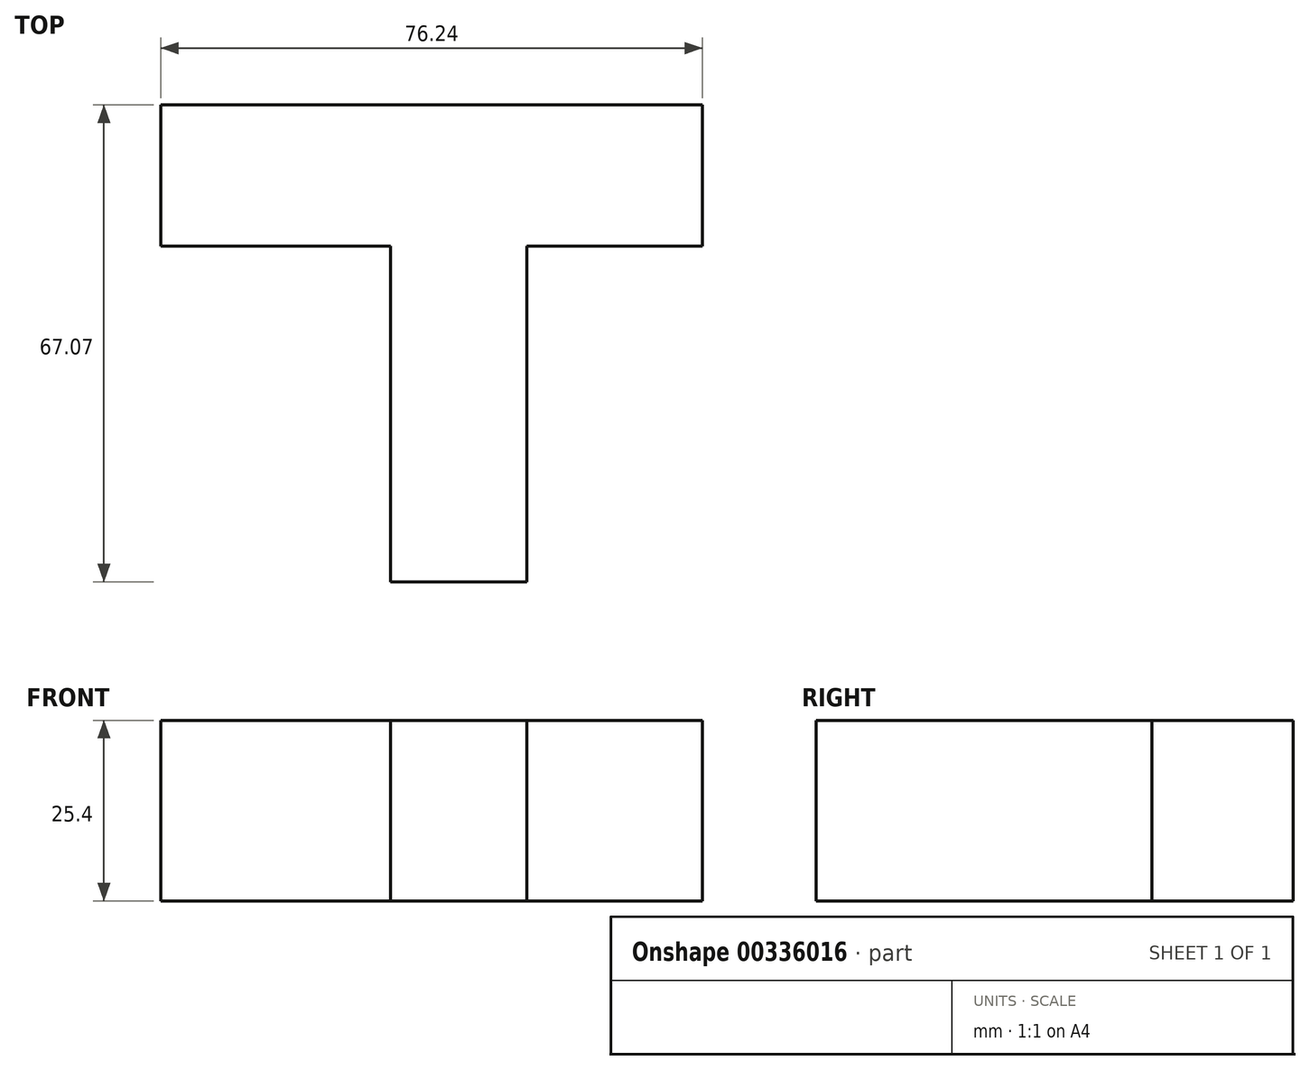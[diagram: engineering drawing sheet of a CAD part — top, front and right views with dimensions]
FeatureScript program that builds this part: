
annotation { "Feature Type Name" : "Feature", "Feature Type Description" : "" }
export const myFeature = defineFeature(function(context is Context, id is Id, definition is map)
    precondition{}
    {
        {
            var Q0;
            Q0=qCreatedBy(makeId("Top.planeOp"),FACE);
            var sketch = newSketch(context, id + "F0", { "sketchPlane" : qUnion([Q0])});
            skLineSegment(sketch, "E0", {"start": v(13.44, -28.7) * mm, "end": v(13.44, 18.55) * mm});
            skLineSegment(sketch, "E1", {"start": v(13.44, 18.55) * mm, "end": v(-18.88, 18.55) * mm});
            skLineSegment(sketch, "E2", {"start": v(-18.88, 18.55) * mm, "end": v(-18.88, 38.58) * mm});
            skLineSegment(sketch, "E3", {"start": v(-18.88, 38.58) * mm, "end": v(57.36, 38.58) * mm});
            skLineSegment(sketch, "E4", {"start": v(57.36, 38.38) * mm, "end": v(57.36, 18.55) * mm});
            skLineSegment(sketch, "E5", {"start": v(57.36, 18.55) * mm, "end": v(32.63, 18.55) * mm});
            skLineSegment(sketch, "E6", {"start": v(32.63, 18.55) * mm, "end": v(32.63, -28.7) * mm});
            skLineSegment(sketch, "E7", {"start": v(13.44, -28.7) * mm, "end": v(32.63, -28.7) * mm});
            skLineSegment(sketch, "E8.bottom", {"start": v(-18.88, 18.55) * mm, "end": v(57.36, 18.55) * mm});
            skLineSegment(sketch, "E8.top", {"start": v(-18.88, 38.38) * mm, "end": v(57.36, 38.38) * mm});
            skLineSegment(sketch, "E8.left", {"start": v(-18.88, 18.55) * mm, "end": v(-18.88, 38.38) * mm});
            skLineSegment(sketch, "E8.right", {"start": v(57.36, 18.55) * mm, "end": v(57.36, 38.38) * mm});
            skSolve(sketch);
        }
        {
            var Q0;
            Q0=makeQuery(id+"F0.imprint","IMPRINT",FACE,{"disambiguationData":[TD([[makeQuery(id+"F0.imprint","IMPRINT",EDGE,{"derivedFrom":sQuery(id+"F0.wireOp",EDGE,"E8.top")}),-1.0]])]});
            var Q1;
            {var subQ0=sQuery(id+"F0.wireOp",EDGE,"E0");Q1=makeQuery(id+"F0.imprint","IMPRINT",FACE,{"disambiguationData":[TD([[makeQuery(id+"F0.imprint","IMPRINT",EDGE,{"derivedFrom":subQ0}),-1.0]])]});}
            extrude(context, id + "F1", {"entities" : qUnion([Q0, Q1]), "depth" : 25.4 * mm});
        }
    });
